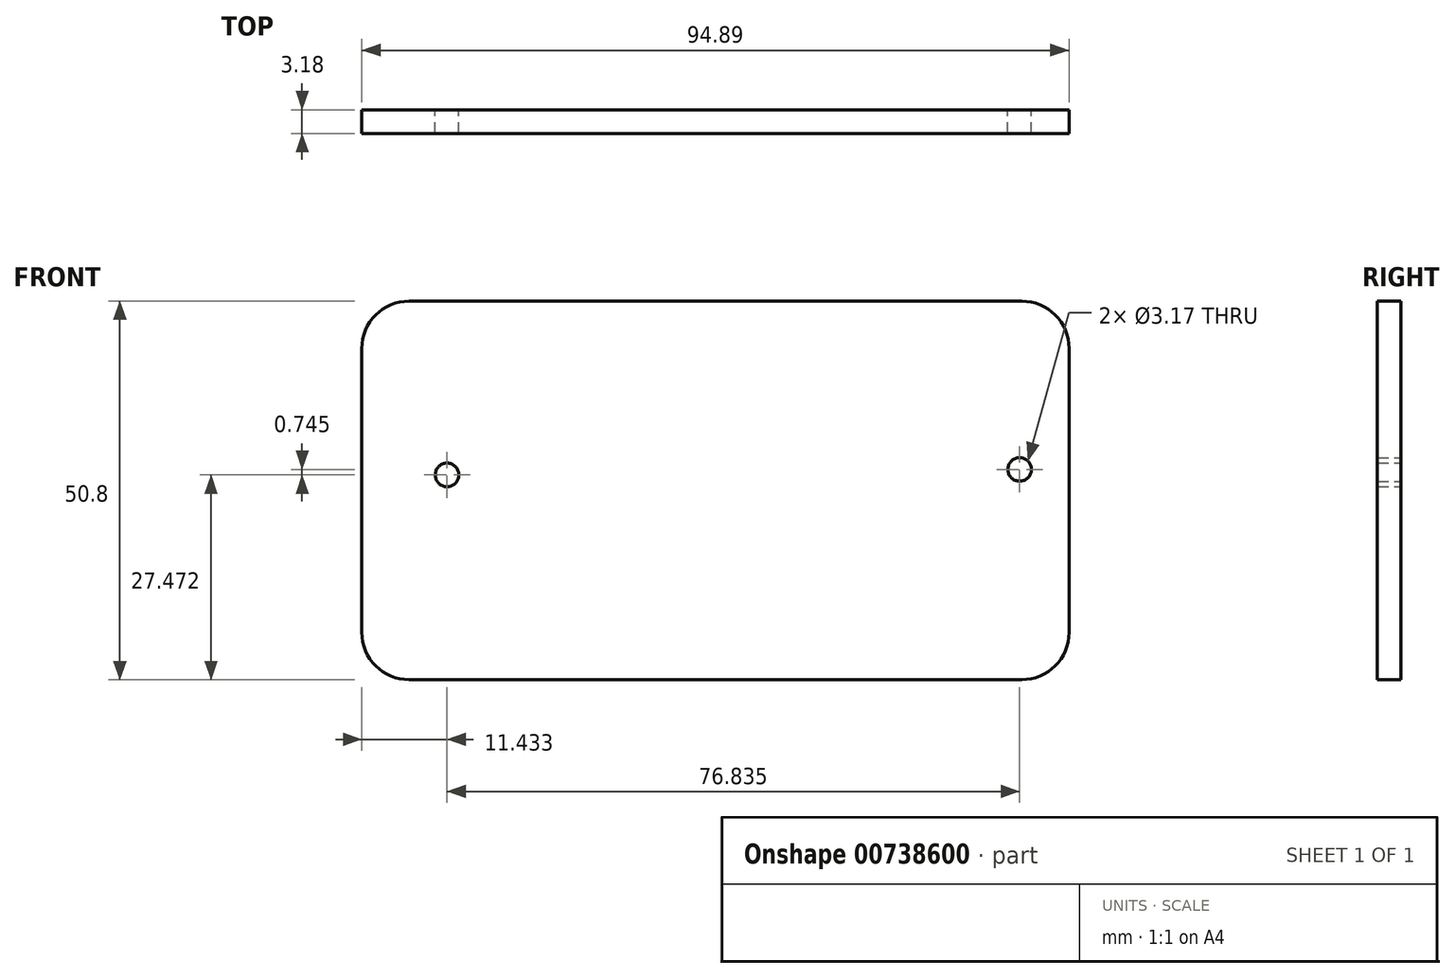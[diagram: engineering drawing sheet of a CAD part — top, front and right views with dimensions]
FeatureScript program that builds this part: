
annotation { "Feature Type Name" : "Feature", "Feature Type Description" : "" }
export const myFeature = defineFeature(function(context is Context, id is Id, definition is map)
    precondition{}
    {
        {
            var Q0;
            Q0=qCreatedBy(makeId("Front.planeOp"),FACE);
            var sketch = newSketch(context, id + "F0", { "sketchPlane" : qUnion([Q0])});
            skLineSegment(sketch, "E0.bottom", {"start": v(-6.35, 6.35) * mm, "end": v(75.84, 6.35) * mm});
            skLineSegment(sketch, "E0.top", {"start": v(-6.35, -44.45) * mm, "end": v(75.84, -44.45) * mm});
            skLineSegment(sketch, "E0.left", {"start": v(-12.7, 0) * mm, "end": v(-12.7, -38.1) * mm});
            skLineSegment(sketch, "E0.right", {"start": v(82.2, 0) * mm, "end": v(82.2, -38.1) * mm});
            skCircle(sketch, "E1", {"center": v(75.57, -16.23) * mm, "radius": 1.59 * mm});
            skCircle(sketch, "E2", {"center": v(-1.27, -16.98) * mm, "radius": 1.59 * mm});
            skPoint(sketch, "E3.visualSharp", {"position": v(82.2, 6.35) * mm});
            skArc(sketch, "E3.filletArc", {"start": v(82.2, 0) * mm, "mid": v(80.33, 4.5) * mm, "end": v(75.84, 6.35) * mm});
            skPoint(sketch, "E4.visualSharp", {"position": v(82.2, -44.45) * mm});
            skArc(sketch, "E4.filletArc", {"start": v(75.84, -44.45) * mm, "mid": v(80.33, -42.6) * mm, "end": v(82.2, -38.1) * mm});
            skPoint(sketch, "E5.visualSharp", {"position": v(-12.7, -44.45) * mm});
            skArc(sketch, "E5.filletArc", {"start": v(-12.7, -38.1) * mm, "mid": v(-10.84, -42.6) * mm, "end": v(-6.35, -44.45) * mm});
            skPoint(sketch, "E6.visualSharp", {"position": v(-12.7, 6.35) * mm});
            skArc(sketch, "E6.filletArc", {"start": v(-6.35, 6.35) * mm, "mid": v(-10.84, 4.5) * mm, "end": v(-12.7, 0) * mm});
            skSolve(sketch);
        }
        {
            var Q0;
            Q0 = qSketchRegion(id + "F0", true);
            extrude(context, id + "F1", {"entities" : qUnion([Q0]), "depth" : 3.17 * mm, "offsetDistance" : 25.4 * mm});
        }
    });
